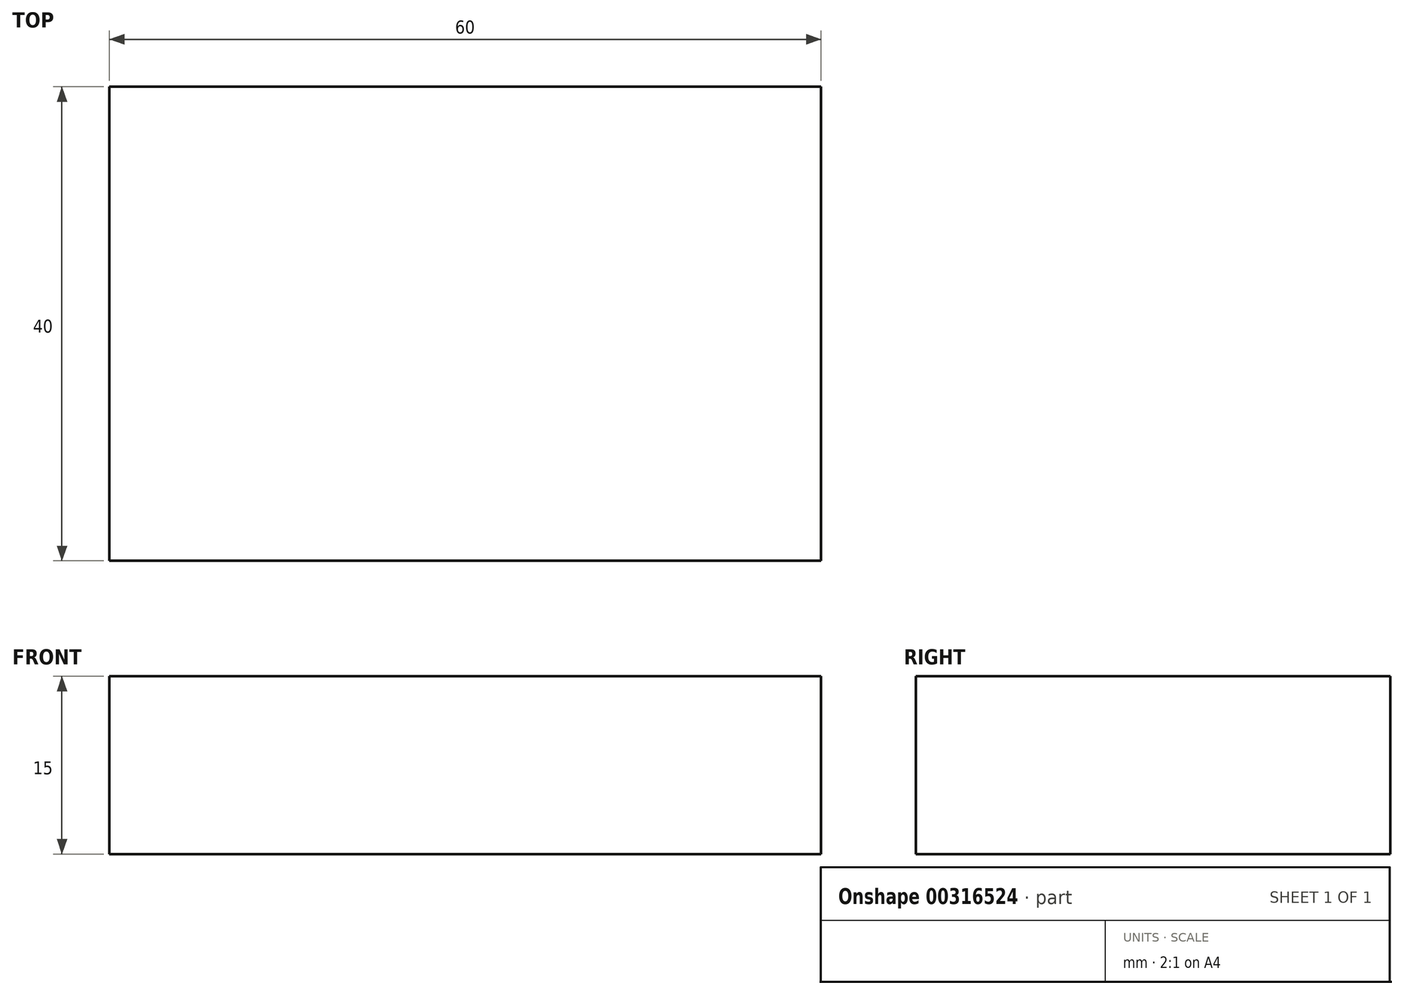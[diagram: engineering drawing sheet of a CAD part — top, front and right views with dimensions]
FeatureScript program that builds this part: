
annotation { "Feature Type Name" : "Feature", "Feature Type Description" : "" }
export const myFeature = defineFeature(function(context is Context, id is Id, definition is map)
    precondition{}
    {
        {
            var Q0;
            Q0=qCreatedBy(makeId("Top.planeOp"),FACE);
            var sketch = newSketch(context, id + "F0", { "sketchPlane" : qUnion([Q0])});
            skLineSegment(sketch, "E0.bottom", {"start": v(-36.5, 24.57) * mm, "end": v(23.5, 24.57) * mm});
            skLineSegment(sketch, "E0.top", {"start": v(-36.5, -15.43) * mm, "end": v(23.5, -15.43) * mm});
            skLineSegment(sketch, "E0.left", {"start": v(-36.5, 24.57) * mm, "end": v(-36.5, -15.43) * mm});
            skLineSegment(sketch, "E0.right", {"start": v(23.5, 24.57) * mm, "end": v(23.5, -15.43) * mm});
            skSolve(sketch);
        }
        {
            var Q0;
            Q0 = qSketchRegion(id + "F0", true);
            extrude(context, id + "F1", {"entities" : qUnion([Q0]), "depth" : 15 * mm});
        }
    });
